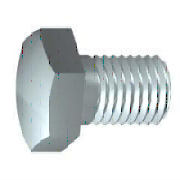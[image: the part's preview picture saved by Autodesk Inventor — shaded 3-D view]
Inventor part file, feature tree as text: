
AUTODESK INVENTOR PART (.ipt)
format: ipt  version: 2023 (Build 270158000, 158)  size: 198,144 bytes
history: native  units: mm
features: sketch x4, other x2, plane x1
ambient origin geometry x8: Origin, YZ Plane, XZ Plane, XY Plane, X Axis, Y Axis, Z Axis, Center Point
bodies: Solid1 (feature_tree)
feature tree (7):
  plane  "Work Plane1"
  sketch  "Sketch1"  dims[d1=6.0mm]
  sketch  "Sketch2"  dims[d61=90.0deg]
  sketch  "Sketch3"  dims[d2=18.0mm]
  other  "Srf1"
  sketch  "Sketch4"  dims[d3=0.0mm d4=0.4mm d62=2.0mm d63=45.0deg d5=7.2mm d6=0.0mm d7=0.0mm d18=0.6mm d8=30.0mm d9=10.0mm d10=4.0mm d11=0.0mm d12=10.0mm d13=4.0mm d14=60.0deg d15=0.0mm d16=6.0mm d17=0.0mm]
  other  "Srf2"
